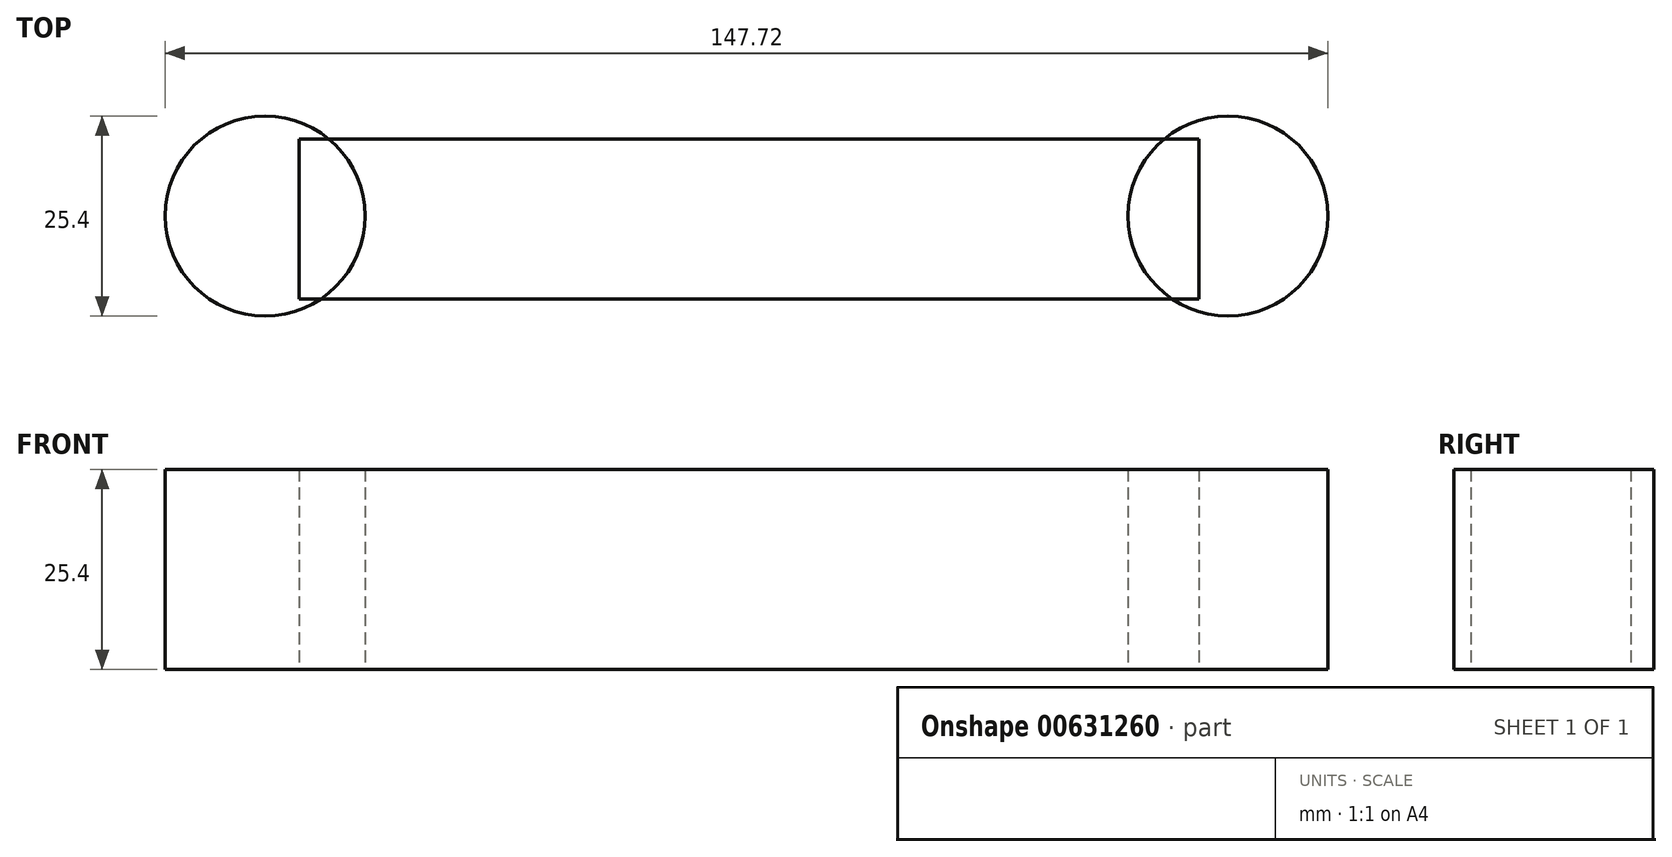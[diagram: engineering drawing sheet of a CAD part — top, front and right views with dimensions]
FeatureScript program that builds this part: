
annotation { "Feature Type Name" : "Feature", "Feature Type Description" : "" }
export const myFeature = defineFeature(function(context is Context, id is Id, definition is map)
    precondition{}
    {
        {
            var Q0;
            Q0=qCreatedBy(makeId("Top.planeOp"),FACE);
            var sketch = newSketch(context, id + "F0", { "sketchPlane" : qUnion([Q0])});
            skLineSegment(sketch, "E0", {"start": v(-41.3, -15.1) * mm, "end": v(73, -15.1) * mm});
            skLineSegment(sketch, "E1", {"start": v(73, -15.1) * mm, "end": v(73, -35.43) * mm});
            skLineSegment(sketch, "E2", {"start": v(73, -35.43) * mm, "end": v(-41.3, -35.43) * mm});
            skLineSegment(sketch, "E3", {"start": v(-41.3, -35.43) * mm, "end": v(-41.3, -15.1) * mm});
            skSolve(sketch);
        }
        {
            var Q0;
            Q0=qCreatedBy(makeId("Top.planeOp"),FACE);
            var sketch = newSketch(context, id + "F1", { "sketchPlane" : qUnion([Q0])});
            skCircle(sketch, "E4", {"center": v(-45.62, -24.9) * mm, "radius": 12.7 * mm});
            skCircle(sketch, "E5", {"center": v(76.7, -24.9) * mm, "radius": 12.7 * mm});
            skSolve(sketch);
        }
        {
            var Q0;
            Q0=makeQuery(id+"F1.imprint","IMPRINT",FACE,{"disambiguationData":[TD([[makeQuery(id+"F1.imprint","IMPRINT",EDGE,{"derivedFrom":sQuery(id+"F1.wireOp",EDGE,"E4")}),1.0]])]});
            var Q1;
            Q1=makeQuery(id+"F1.imprint","IMPRINT",FACE,{"disambiguationData":[TD([[makeQuery(id+"F1.imprint","IMPRINT",EDGE,{"derivedFrom":sQuery(id+"F1.wireOp",EDGE,"E5")}),1.0]])]});
            var Q2;
            Q2=makeQuery(id+"F0.imprint","IMPRINT",FACE,{"disambiguationData":[TD([[makeQuery(id+"F0.imprint","IMPRINT",EDGE,{"derivedFrom":sQuery(id+"F0.wireOp",EDGE,"E0")}),-1.0]])]});
            extrude(context, id + "F2", {"entities" : qUnion([Q0, Q1, Q2]), "depth" : 25.4 * mm, "offsetDistance" : 25.4 * mm});
        }
    });
